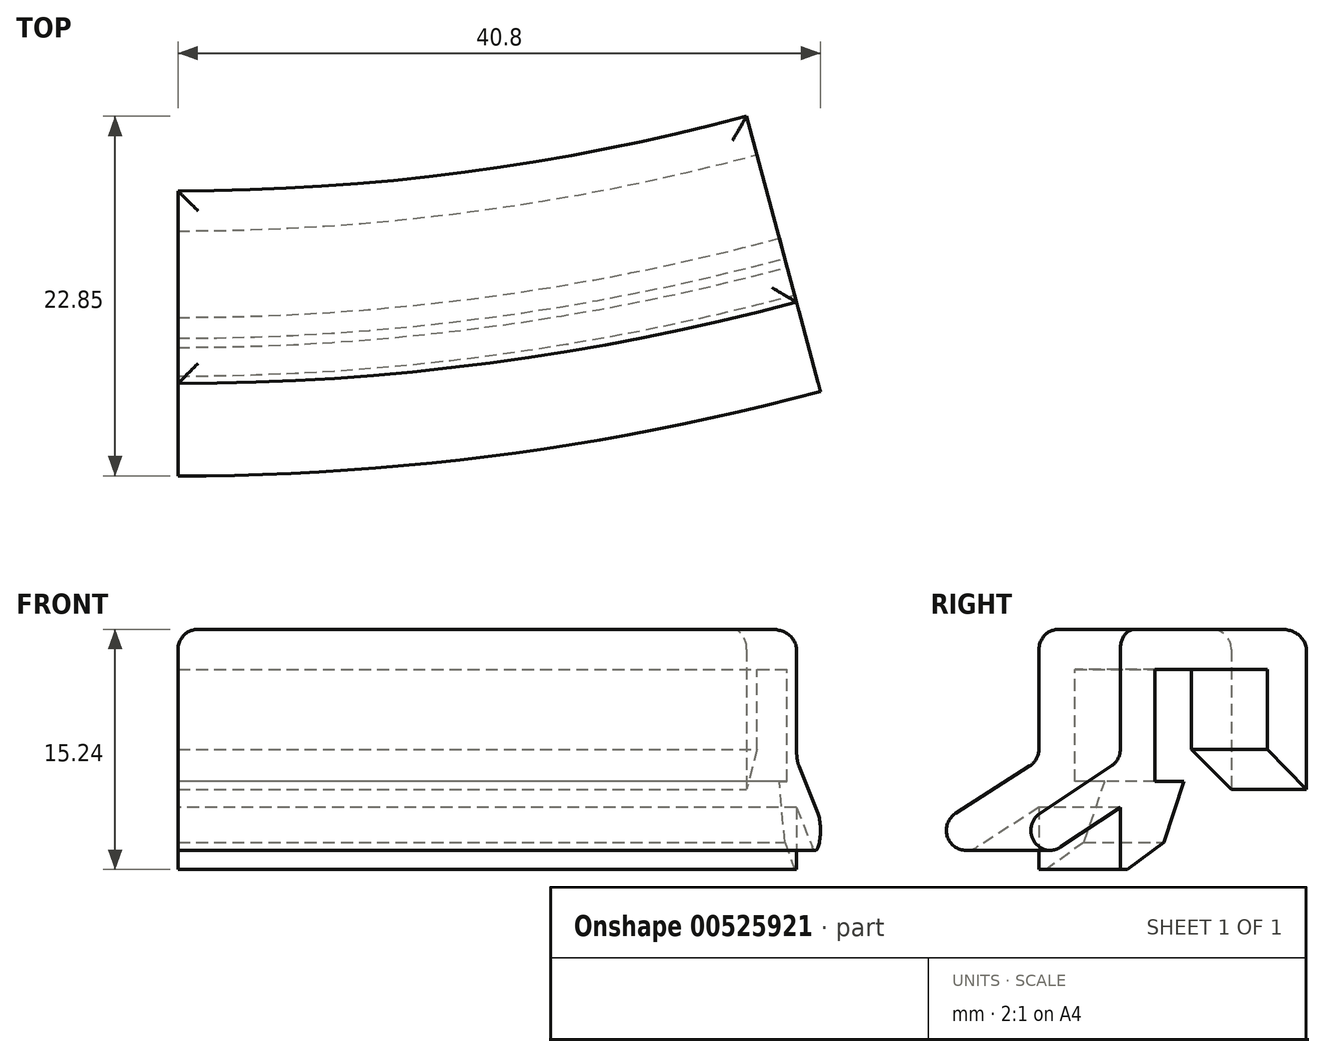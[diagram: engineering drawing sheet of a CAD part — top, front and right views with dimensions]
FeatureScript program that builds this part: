
annotation { "Feature Type Name" : "Feature", "Feature Type Description" : "" }
export const myFeature = defineFeature(function(context is Context, id is Id, definition is map)
    precondition{}
    {
        {
            var Q0;
            Q0=qCreatedBy(makeId("Top.planeOp"),FACE);
            var sketch = newSketch(context, id + "F0", { "sketchPlane" : qUnion([Q0])});
            skCircle(sketch, "E0", {"center": v(0, 0) * mm, "radius": 149.23 * mm});
            skCircle(sketch, "E1", {"center": v(0, 0) * mm, "radius": 142.08 * mm});
            skSolve(sketch);
        }
        {
            var Q0;
            Q0=qCreatedBy(makeId("Top.planeOp"),FACE);
            var sketch = newSketch(context, id + "F1", { "sketchPlane" : qUnion([Q0])});
            skLineSegment(sketch, "E2", {"start": v(0, -139.54) * mm, "end": v(0, -151.77) * mm});
            skLineSegment(sketch, "E3", {"start": v(36.12, -134.79) * mm, "end": v(39.28, -146.6) * mm});
            skArc(sketch, "E4.0", {"start": v(0, -149.23) * mm, "mid": v(19.48, -147.95) * mm, "end": v(38.62, -144.14) * mm});
            skArc(sketch, "E5.0", {"start": v(0, -142.08) * mm, "mid": v(18.55, -140.87) * mm, "end": v(36.77, -137.24) * mm});
            skArc(sketch, "E6.0", {"start": v(0, -139.54) * mm, "mid": v(18.21, -138.35) * mm, "end": v(36.12, -134.79) * mm});
            skArc(sketch, "E7.0", {"start": v(0, -151.77) * mm, "mid": v(19.8, -150.47) * mm, "end": v(39.28, -146.6) * mm});
            skSolve(sketch);
        }
        {
            var Q0;
            Q0 = qSketchRegion(id + "F1", true);
            extrude(context, id + "F2", {"entities" : qUnion([Q0]), "depth" : 2.54 * mm, "offsetDistance" : 25.4 * mm});
        }
        {
            var Q0;
            {var subQ2=sQuery(id+"F1.wireOp",EDGE,"E5.0");Q0=makeQuery(id+"F1.imprint","IMPRINT",FACE,{"disambiguationData":[TD([[makeQuery(id+"F1.imprint","IMPRINT",EDGE,{"derivedFrom":subQ2}),1.0]])]});}
            extrude(context, id + "F3", {"entities" : qUnion([Q0]), "operationType" : NewBodyOperationType.ADD, "oppositeDirection" : true, "depth" : 7.62 * mm, "offsetDistance" : 25.4 * mm});
        }
        {
            var Q0;
            {var subQ2=sQuery(id+"F1.wireOp",EDGE,"E4.0");Q0=makeQuery(id+"F1.imprint","IMPRINT",FACE,{"disambiguationData":[TD([[makeQuery(id+"F1.imprint","IMPRINT",EDGE,{"derivedFrom":subQ2}),-1.0]])]});}
            var sketch = newSketch(context, id + "F4", { "sketchPlane" : qUnion([Q0])});
            skArc(sketch, "E8.0", {"start": v(0, -149.48) * mm, "mid": v(19.51, -148.2) * mm, "end": v(38.69, -144.39) * mm});
            skLineSegment(sketch, "E9.0", {"start": v(0, -149.48) * mm, "end": v(0, -151.77) * mm});
            skArc(sketch, "E10.0", {"start": v(0, -151.77) * mm, "mid": v(19.8, -150.47) * mm, "end": v(39.28, -146.6) * mm});
            skLineSegment(sketch, "E11.0", {"start": v(38.69, -144.39) * mm, "end": v(39.28, -146.6) * mm});
            skPoint(sketch, "E12.orphan", {"position": v(36.12, -134.79) * mm});
            skPoint(sketch, "E13.0.end.orphan", {"position": v(38.62, -144.14) * mm});
            skPoint(sketch, "E13.0.start.orphan", {"position": v(0, -149.23) * mm});
            skPoint(sketch, "E14.orphan", {"position": v(0, -139.54) * mm});
            skSolve(sketch);
        }
        {
            var Q0;
            Q0=makeQuery(id+"F4.imprint","IMPRINT",FACE,{"disambiguationData":[TD([[makeQuery(id+"F4.imprint","IMPRINT",EDGE,{"derivedFrom":sQuery(id+"F4.wireOp",EDGE,"E8.0")}),-1.0]])]});
            extrude(context, id + "F5", {"entities" : qUnion([Q0]), "operationType" : NewBodyOperationType.ADD, "oppositeDirection" : true, "depth" : 12.7 * mm, "offsetDistance" : 25.4 * mm});
        }
        {
            var Q0;
            {var subQ0=sQuery(id+"F1.wireOp",EDGE,"E2");Q0=makeQuery(id+"F5.boolean.opBoolean","MERGE",FACE,{"derivedFrom":[makeQuery(id+"F3.boolean.opBoolean","MERGE",FACE,{"derivedFrom":[makeQuery(id+"F2.opExtrude","SWEPT_FACE",FACE,{"disambiguationData":[OSD([subQ0])]}),makeQuery(id+"F3.opExtrude","SWEPT_FACE",FACE,{"disambiguationData":[OSD([subQ0])]})]}),makeQuery(id+"F5.opExtrude","SWEPT_FACE",FACE,{"disambiguationData":[OSD([sQuery(id+"F4.wireOp",EDGE,"E9.0")])]})]});}
            var sketch = newSketch(context, id + "F6", { "sketchPlane" : qUnion([Q0])});
            skLineSegment(sketch, "E15.0", {"start": v(149.48, -12.7) * mm, "end": v(149.48, -7.11) * mm});
            skLineSegment(sketch, "E16", {"start": v(149.48, -12.7) * mm, "end": v(147.57, -7.11) * mm});
            skLineSegment(sketch, "E17", {"start": v(147.57, -7.11) * mm, "end": v(149.48, -7.11) * mm});
            skPoint(sketch, "E18.orphan", {"position": v(149.48, 0) * mm});
            skSolve(sketch);
        }
        {
            var Q0;
            Q0=makeQuery(id+"F6.imprint","IMPRINT",FACE,{"disambiguationData":[TD([[makeQuery(id+"F6.imprint","IMPRINT",EDGE,{"derivedFrom":sQuery(id+"F6.wireOp",EDGE,"E15.0")}),1.0]])]});
            var Q1;
            Q1=sQuery(id+"F0.wireOp",EDGE,"E1");
            revolve(context, id + "F7", {"operationType" : NewBodyOperationType.ADD, "entities" : qUnion([Q0]), "axis" : qUnion([Q1]), "revolveType" : RevolveType.ONE_DIRECTION, "angle" : 15 * degree});
        }
        {
            var Q0;
            Q0=makeQuery(id+"F3.opExtrude","CAP_EDGE",EDGE,{"disambiguationData":[OSD([sQuery(id+"F1.wireOp",EDGE,"E5.0")])],"isStart":false});
            var Q1;
            Q1=makeQuery(id+"F5.opExtrude","CAP_EDGE",EDGE,{"disambiguationData":[OSD([sQuery(id+"F4.wireOp",EDGE,"E8.0")])],"isStart":false});
            chamfer(context, id + "F8", {"entities" : qUnion([Q0, Q1]), "width" : 2.54 * mm, "tangentPropagation" : true});
        }
        {
            var Q0;
            {var subQ0=sQuery(id+"F1.wireOp",EDGE,"E2");Q0=makeQuery(id+"F7.boolean.opBoolean","MERGE",FACE,{"derivedFrom":[makeQuery(id+"F5.boolean.opBoolean","MERGE",FACE,{"derivedFrom":[makeQuery(id+"F3.boolean.opBoolean","MERGE",FACE,{"derivedFrom":[makeQuery(id+"F2.opExtrude","SWEPT_FACE",FACE,{"disambiguationData":[OSD([subQ0])]}),makeQuery(id+"F3.opExtrude","SWEPT_FACE",FACE,{"disambiguationData":[OSD([subQ0])]})]}),makeQuery(id+"F5.opExtrude","SWEPT_FACE",FACE,{"disambiguationData":[OSD([sQuery(id+"F4.wireOp",EDGE,"E9.0")])]})]}),makeQuery(id+"F7.opRevolve","CAP_FACE",FACE,{"disambiguationData":[OSD([sQuery(id+"F6.wireOp",EDGE,"E15.0"),sQuery(id+"F6.wireOp",EDGE,"E16"),sQuery(id+"F6.wireOp",EDGE,"E17")])],"isStart":true})]});}
            var sketch = newSketch(context, id + "F9", { "sketchPlane" : qUnion([Q0])});
            skLineSegment(sketch, "E19", {"start": v(151.77, -5.76) * mm, "end": v(151.77, -8.77) * mm});
            skLineSegment(sketch, "E20", {"start": v(151.77, -8.77) * mm, "end": v(156.76, -11.98) * mm});
            skLineSegment(sketch, "E21", {"start": v(156.76, -11.98) * mm, "end": v(158.13, -9.84) * mm});
            skLineSegment(sketch, "E22", {"start": v(158.13, -9.84) * mm, "end": v(151.77, -5.76) * mm});
            skSolve(sketch);
        }
        {
            var Q0;
            Q0=makeQuery(id+"F9.imprint","IMPRINT",FACE,{"disambiguationData":[TD([[makeQuery(id+"F9.imprint","IMPRINT",EDGE,{"derivedFrom":sQuery(id+"F9.wireOp",EDGE,"E19")}),1.0]])]});
            var Q1;
            Q1=sQuery(id+"F0.wireOp",EDGE,"E1");
            revolve(context, id + "F10", {"operationType" : NewBodyOperationType.ADD, "entities" : qUnion([Q0]), "axis" : qUnion([Q1]), "revolveType" : RevolveType.ONE_DIRECTION, "angle" : 15 * degree});
        }
        {
            var Q0;
            Q0=makeQuery(id+"F10.opRevolve","SWEPT_EDGE",EDGE,{"disambiguationData":[OSD([sQuery(id+"F1.wireOp",EDGE,"E2"),sQuery(id+"F1.wireOp",EDGE,"E7.0"),sQuery(id+"F4.wireOp",EDGE,"E9.0"),sQuery(id+"F4.wireOp",EDGE,"E10.0"),sQuery(id+"F9.wireOp",EDGE,"E19"),sQuery(id+"F9.wireOp",EDGE,"E22")])]});
            var Q1;
            Q1=makeQuery(id+"F10.opRevolve","SWEPT_EDGE",EDGE,{"disambiguationData":[OSD([sQuery(id+"F9.wireOp",EDGE,"E21"),sQuery(id+"F9.wireOp",EDGE,"E22")])]});
            var Q2;
            Q2=makeQuery(id+"F10.opRevolve","SWEPT_EDGE",EDGE,{"disambiguationData":[OSD([sQuery(id+"F9.wireOp",EDGE,"E20"),sQuery(id+"F9.wireOp",EDGE,"E21")])]});
            var Q3;
            Q3=makeQuery(id+"F10.opRevolve","SWEPT_EDGE",EDGE,{"disambiguationData":[OSD([sQuery(id+"F1.wireOp",EDGE,"E2"),sQuery(id+"F1.wireOp",EDGE,"E7.0"),sQuery(id+"F4.wireOp",EDGE,"E9.0"),sQuery(id+"F4.wireOp",EDGE,"E10.0"),sQuery(id+"F9.wireOp",EDGE,"E19"),sQuery(id+"F9.wireOp",EDGE,"E20")])]});
            var Q4;
            Q4=makeQuery(id+"F2.opExtrude","CAP_EDGE",EDGE,{"disambiguationData":[OSD([sQuery(id+"F1.wireOp",EDGE,"E7.0")])],"isStart":false});
            var Q5;
            Q5=makeQuery(id+"F2.opExtrude","CAP_EDGE",EDGE,{"disambiguationData":[OSD([sQuery(id+"F1.wireOp",EDGE,"E6.0")])],"isStart":false});
            var Q6;
            Q6=makeQuery(id+"F2.opExtrude","CAP_EDGE",EDGE,{"disambiguationData":[OSD([sQuery(id+"F1.wireOp",EDGE,"E2")])],"isStart":false});
            var Q7;
            Q7=makeQuery(id+"F2.opExtrude","CAP_EDGE",EDGE,{"disambiguationData":[OSD([sQuery(id+"F1.wireOp",EDGE,"E3")])],"isStart":false});
            fillet(context, id + "F11", {"entities" : qUnion([Q0, Q1, Q2, Q3, Q4, Q5, Q6, Q7]), "radius" : 1.27 * mm, "tangentPropagation" : true, "allowEdgeOverflow" : false});
        }
    });
